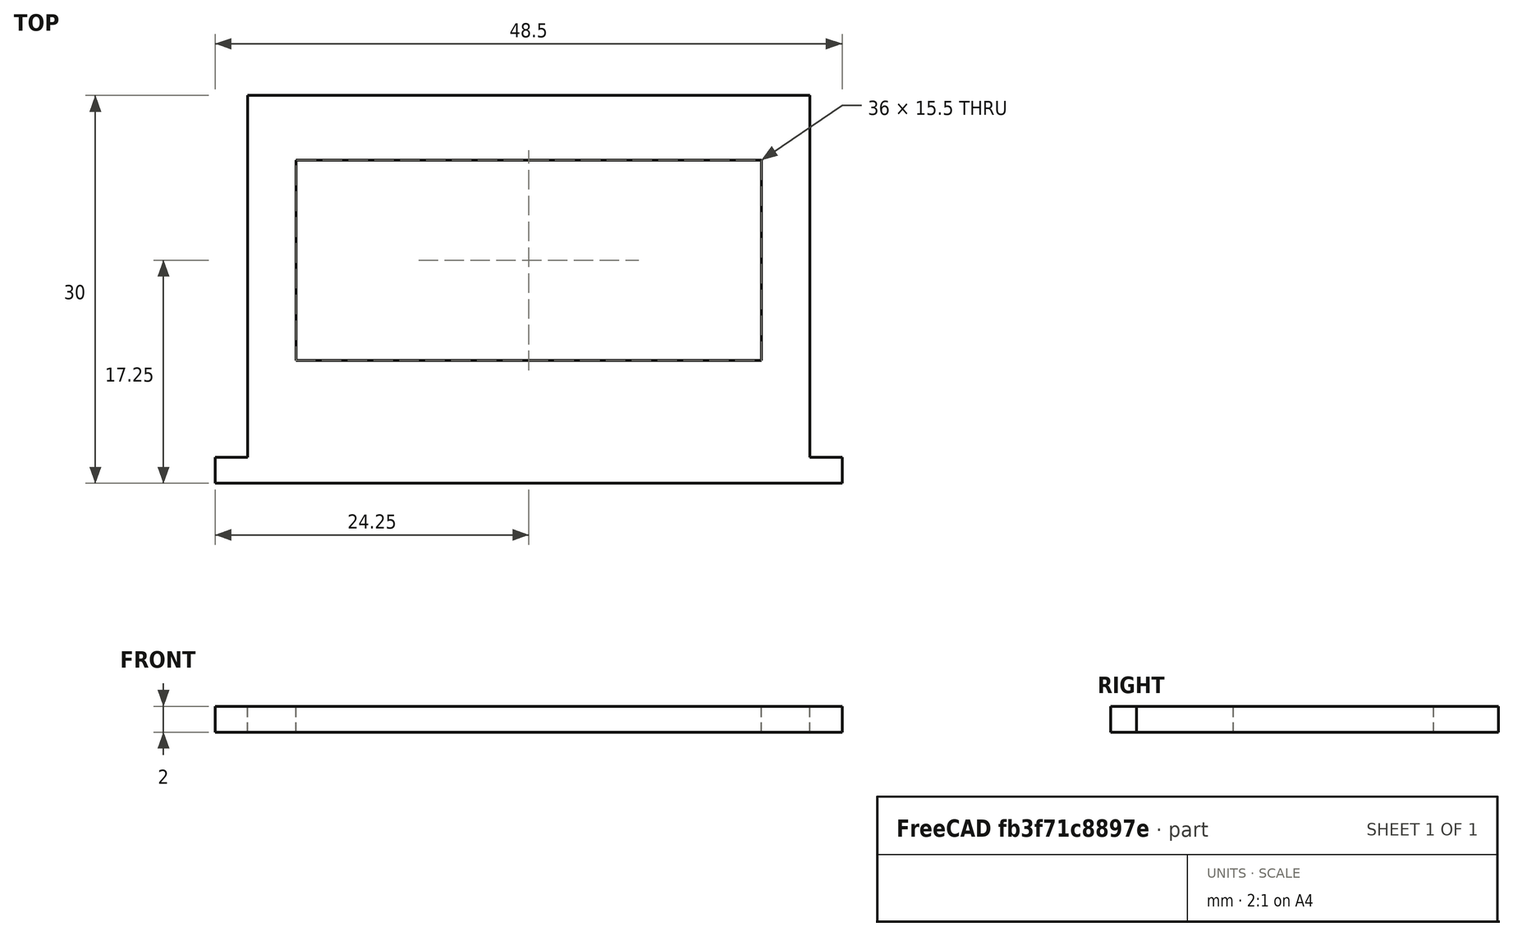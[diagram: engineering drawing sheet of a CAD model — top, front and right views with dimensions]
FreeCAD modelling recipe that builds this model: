
FCSTD DOCUMENT  (FreeCAD 0.19R)
Label: power-bank-mount-insert
License: All rights reserved
LicenseURL: http://en.wikipedia.org/wiki/All_rights_reserved
objects: Sketcher::SketchObject×1, PartDesign::Pad×1, PartDesign::Body×1, Mesh::Feature×1
note: 4 computed .brp shape members not serialized (recipe doc carries the construction recipe); baked Part::Feature solids carry a one-line shape summary decoded from their .brp

FEATURE [Sketcher::SketchObject] Sketch
  FullyConstrained = true
  MapMode = 5
  Support = -> [XY_Plane]
  sketch-geometry (18):
    g0: LineSegment StartX=0 StartY=0 StartZ=0 EndX=48.5 EndY=0 EndZ=0
    g1: LineSegment StartX=48.5 StartY=0 StartZ=0 EndX=48.5 EndY=2 EndZ=0
    g2: LineSegment StartX=48.5 StartY=2 StartZ=0 EndX=46 EndY=2 EndZ=0
    g3: LineSegment StartX=46 StartY=2 StartZ=0 EndX=46 EndY=30 EndZ=0
    g4: LineSegment StartX=46 StartY=30 StartZ=0 EndX=2.5 EndY=30 EndZ=0
    g5: LineSegment StartX=2.5 StartY=30 StartZ=0 EndX=2.5 EndY=2 EndZ=0
    g6: LineSegment StartX=2.5 StartY=2 StartZ=0 EndX=0 EndY=2 EndZ=0
    g7: LineSegment StartX=0 StartY=2 StartZ=0 EndX=0 EndY=0 EndZ=0
    g8: LineSegment StartX=6.25 StartY=25 StartZ=0 EndX=42.25 EndY=25 EndZ=0
    g9: LineSegment StartX=42.25 StartY=25 StartZ=0 EndX=42.25 EndY=9.5 EndZ=0
    g10: LineSegment StartX=42.25 StartY=9.5 StartZ=0 EndX=6.25 EndY=9.5 EndZ=0
    g11: LineSegment StartX=6.25 StartY=9.5 StartZ=0 EndX=6.25 EndY=25 EndZ=0
    g12: LineSegment StartX=24.25 StartY=25 StartZ=0 EndX=24.25 EndY=30 EndZ=0
    g13: LineSegment StartX=2.5 StartY=30 StartZ=0 EndX=46 EndY=30 EndZ=0
    g14: LineSegment StartX=46 StartY=30 StartZ=0 EndX=46 EndY=4.5 EndZ=0
    g15: LineSegment StartX=46 StartY=4.5 StartZ=0 EndX=2.5 EndY=4.5 EndZ=0
    g16: LineSegment StartX=2.5 StartY=4.5 StartZ=0 EndX=2.5 EndY=30 EndZ=0
    g17: LineSegment StartX=42.25 StartY=17.25 StartZ=0 EndX=46 EndY=17.25 EndZ=0
  constraints (50):
    c: Coincident(g0,g-1)
    c: PointOnObject(g0,g-1)
    c: Coincident(g1,g0)
    c: Vertical(g1)
    c: Coincident(g2,g1)
    c: Horizontal(g2)
    c: Coincident(g3,g2)
    c: Vertical(g3)
    c: Coincident(g4,g3)
    c: Horizontal(g4)
    c: Coincident(g5,g4)
    c: Vertical(g5)
    c: Coincident(g6,g5)
    c: PointOnObject(g6,g-2)
    c: Horizontal(g6)
    c: Coincident(g7,g6)
    c: Coincident(g7,g0)
    c: Equal(g7,g1)
    c: Equal(g6,g2)
    c: DistanceX(g4,g4) = 43.5
    c: DistanceX(g0,g0) = 48.5
    c: DistanceY(g1,g1) = 2
    c: DistanceY(g3,g3) = 28
    c: Coincident(g8,g9)
    c: Coincident(g9,g10)
    c: Coincident(g10,g11)
    c: Coincident(g11,g8)
    c: Horizontal(g8)
    c: Horizontal(g10)
    c: Vertical(g9)
    c: Vertical(g11)
    c: Symmetric(g3,g4,g12)
    c: Symmetric(g8,g8,g12)
    c: Vertical(g12)
    c: DistanceX(g10,g10) = 36
    c: DistanceY(g11,g11) = 15.5
    c: Coincident(g13,g14)
    c: Coincident(g14,g15)
    c: Coincident(g15,g16)
    c: Coincident(g16,g13)
    c: Horizontal(g13)
    c: Horizontal(g15)
    c: Vertical(g14)
    c: Vertical(g16)
    c: Coincident(g13,g4)
    c: PointOnObject(g14,g3)
    c: DistanceY(g15,g4) = 25.5
    c: Horizontal(g17)
    c: Symmetric(g9,g8,g17)
    c: Symmetric(g14,g3,g17)
FEATURE [PartDesign::Pad] Pad
  Direction = (1,1,1)
  Length = 2
  Length2 = 100
  Profile = -> Sketch
  Type = 0
FEATURE [PartDesign::Body] Body
  Group = -> [Sketch,Pad]
  Origin = -> Origin
  Tip = -> Pad
FEATURE [Mesh::Feature] Mesh  label="Body (Meshed)"
